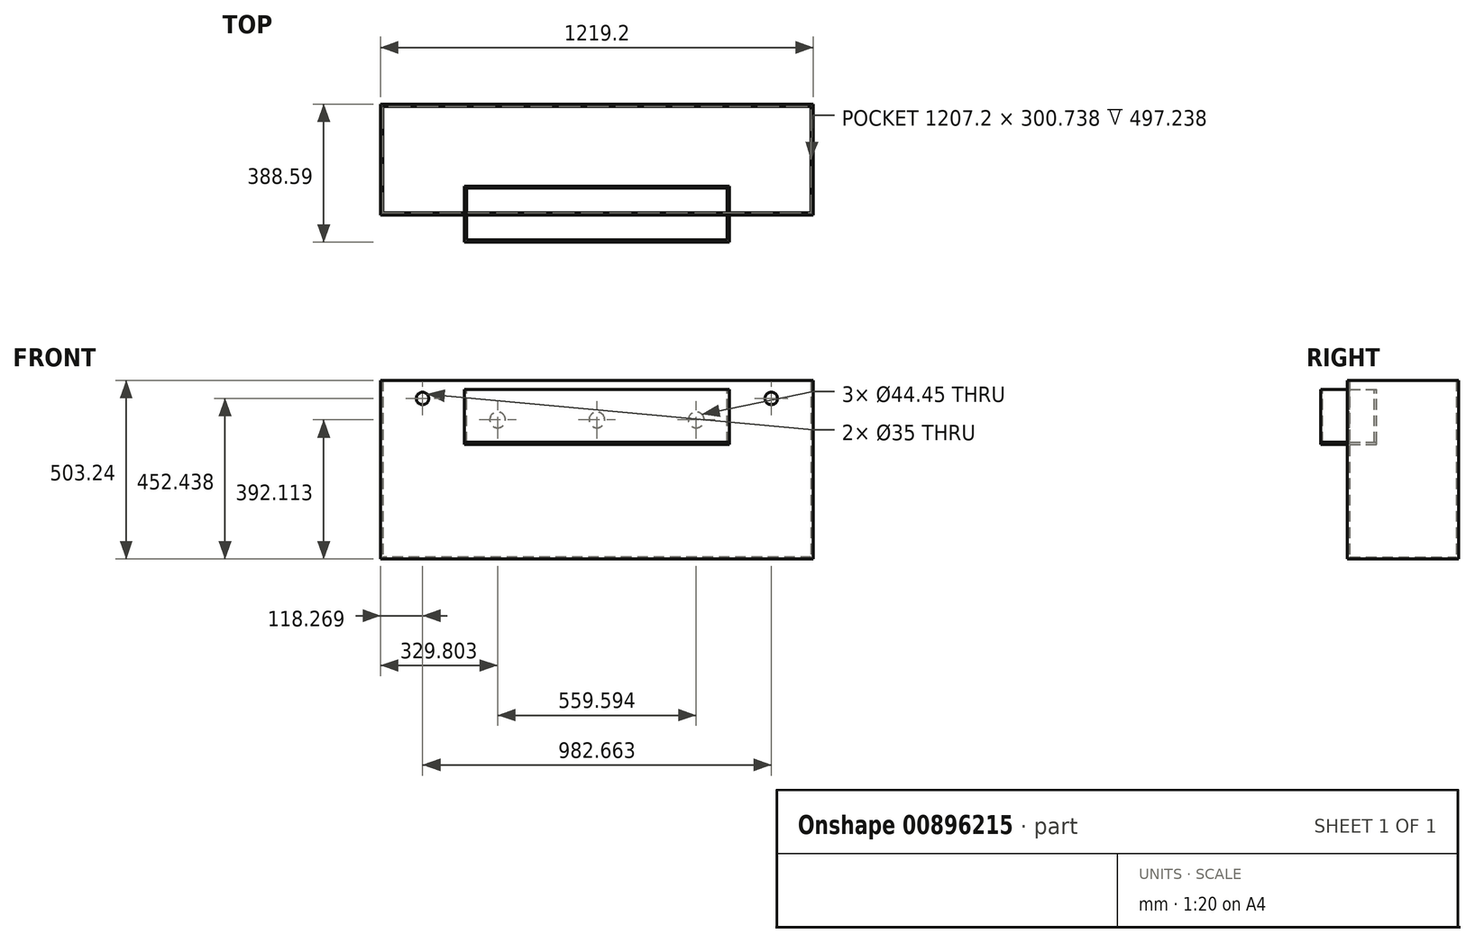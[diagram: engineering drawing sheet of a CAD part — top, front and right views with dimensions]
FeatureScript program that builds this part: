
annotation { "Feature Type Name" : "Feature", "Feature Type Description" : "" }
export const myFeature = defineFeature(function(context is Context, id is Id, definition is map)
    precondition{}
    {
        {
            var Q0;
            Q0=qCreatedBy(makeId("Top.planeOp"),FACE);
            var sketch = newSketch(context, id + "F0", { "sketchPlane" : qUnion([Q0])});
            skLineSegment(sketch, "E0.bottom", {"start": v(609.6, -156.37) * mm, "end": v(-609.6, -156.37) * mm});
            skLineSegment(sketch, "E0.top", {"start": v(609.6, 156.37) * mm, "end": v(-609.6, 156.37) * mm});
            skLineSegment(sketch, "E0.left", {"start": v(609.6, -156.37) * mm, "end": v(609.6, 156.37) * mm});
            skLineSegment(sketch, "E0.right", {"start": v(-609.6, -156.37) * mm, "end": v(-609.6, 156.37) * mm});
            skPoint(sketch, "E0.middle", {"position": v(0, 0) * mm});
            skSolve(sketch);
        }
        {
            var Q0;
            Q0=makeQuery(id+"F0.imprint","IMPRINT",FACE,{"disambiguationData":[TD([[makeQuery(id+"F0.imprint","IMPRINT",EDGE,{"derivedFrom":sQuery(id+"F0.wireOp",EDGE,"E0.bottom")}),-1.0]])]});
            extrude(context, id + "F1", {"entities" : qUnion([Q0]), "depth" : 503.24 * mm});
        }
        {
            var Q0;
            Q0=makeQuery(id+"F1.opExtrude","CAP_FACE",FACE,{"disambiguationData":[OSD([sQuery(id+"F0.wireOp",EDGE,"E0.bottom"),sQuery(id+"F0.wireOp",EDGE,"E0.top"),sQuery(id+"F0.wireOp",EDGE,"E0.left"),sQuery(id+"F0.wireOp",EDGE,"E0.right")])],"isStart":false});
            shell(context, id + "F2", {"entities" : qUnion([Q0]), "thickness" : 6 * mm});
        }
        {
            var Q0;
            Q0=makeQuery(id+"F1.opExtrude","SWEPT_FACE",FACE,{"disambiguationData":[OSD([sQuery(id+"F0.wireOp",EDGE,"E0.bottom")])]});
            var sketch = newSketch(context, id + "F3", { "sketchPlane" : qUnion([Q0])});
            skPoint(sketch, "E1", {"position": v(609.6, 414.34) * mm});
            skPoint(sketch, "E2", {"position": v(-609.6, 414.34) * mm});
            skLineSegment(sketch, "E3", {"start": v(-609.6, 414.34) * mm, "end": v(609.6, 414.34) * mm, "construction": true});
            skLineSegment(sketch, "E4", {"start": v(0, 503.24) * mm, "end": v(0, 0) * mm, "construction": true});
            skLineSegment(sketch, "E5", {"start": v(-609.6, 369.89) * mm, "end": v(609.6, 369.89) * mm, "construction": true});
            skLineSegment(sketch, "E6", {"start": v(-373.06, 503.24) * mm, "end": v(-373.06, 0) * mm, "construction": true});
            skLineSegment(sketch, "E7", {"start": v(373.06, 503.24) * mm, "end": v(373.06, 0) * mm, "construction": true});
            skLineSegment(sketch, "E8", {"start": v(0, 414.34) * mm, "end": v(0, 369.89) * mm, "construction": true});
            skPoint(sketch, "E9", {"position": v(0, 392.11) * mm});
            skLineSegment(sketch, "E10", {"start": v(-609.6, 392.11) * mm, "end": v(609.6, 392.11) * mm, "construction": true});
            skCircle(sketch, "E11", {"center": v(0, 392.11) * mm, "radius": 22.22 * mm});
            skLineSegment(sketch, "E12", {"start": v(0, 414.34) * mm, "end": v(-373.06, 414.34) * mm, "construction": true});
            skPoint(sketch, "E13", {"position": v(-186.53, 414.34) * mm});
            skLineSegment(sketch, "E14", {"start": v(-186.53, 414.34) * mm, "end": v(-186.53, 369.89) * mm, "construction": true});
            skLineSegment(sketch, "E15", {"start": v(0, 414.34) * mm, "end": v(373.06, 414.34) * mm, "construction": true});
            skPoint(sketch, "E16", {"position": v(186.53, 414.34) * mm});
            skLineSegment(sketch, "E17", {"start": v(186.53, 414.34) * mm, "end": v(186.53, 369.89) * mm, "construction": true});
            skLineSegment(sketch, "E18", {"start": v(-186.53, 414.34) * mm, "end": v(-373.06, 414.34) * mm, "construction": true});
            skPoint(sketch, "E19", {"position": v(-279.8, 414.34) * mm});
            skLineSegment(sketch, "E20", {"start": v(-279.8, 414.34) * mm, "end": v(-279.8, 369.89) * mm, "construction": true});
            skCircle(sketch, "E21", {"center": v(-279.8, 392.11) * mm, "radius": 22.23 * mm});
            skLineSegment(sketch, "E22", {"start": v(186.53, 414.34) * mm, "end": v(373.06, 414.34) * mm, "construction": true});
            skPoint(sketch, "E23", {"position": v(279.8, 414.34) * mm});
            skLineSegment(sketch, "E24", {"start": v(279.8, 414.34) * mm, "end": v(279.8, 369.89) * mm, "construction": true});
            skCircle(sketch, "E25", {"center": v(279.8, 392.11) * mm, "radius": 22.22 * mm});
            skLineSegment(sketch, "E26", {"start": v(-609.6, 328.61) * mm, "end": v(609.6, 328.61) * mm, "construction": true});
            skLineSegment(sketch, "E27", {"start": v(373.06, 503.24) * mm, "end": v(609.6, 503.24) * mm, "construction": true});
            skLineSegment(sketch, "E28", {"start": v(491.33, 503.24) * mm, "end": v(491.33, 0) * mm, "construction": true});
            skLineSegment(sketch, "E29", {"start": v(-609.6, 503.24) * mm, "end": v(-373.06, 503.24) * mm, "construction": true});
            skLineSegment(sketch, "E30", {"start": v(-491.33, 503.24) * mm, "end": v(-491.33, 0) * mm, "construction": true});
            skLineSegment(sketch, "E31", {"start": v(-609.6, 503.24) * mm, "end": v(-609.6, 414.34) * mm, "construction": true});
            skCircle(sketch, "E32", {"center": v(491.33, 452.44) * mm, "radius": 17.5 * mm});
            skLineSegment(sketch, "E33", {"start": v(-609.6, 452.44) * mm, "end": v(609.6, 452.44) * mm, "construction": true});
            skCircle(sketch, "E34", {"center": v(-491.33, 452.44) * mm, "radius": 17.5 * mm});
            skSolve(sketch);
        }
        {
            var Q0;
            Q0=makeQuery(id+"F1.opExtrude","CAP_FACE",FACE,{"disambiguationData":[OSD([sQuery(id+"F0.wireOp",EDGE,"E0.bottom"),sQuery(id+"F0.wireOp",EDGE,"E0.top"),sQuery(id+"F0.wireOp",EDGE,"E0.left"),sQuery(id+"F0.wireOp",EDGE,"E0.right")])],"isStart":false});
            var sketch = newSketch(context, id + "F4", { "sketchPlane" : qUnion([Q0])});
            skLineSegment(sketch, "E35", {"start": v(-603.6, -80.52) * mm, "end": v(603.6, -80.52) * mm, "construction": true});
            skPoint(sketch, "E36.0", {"position": v(373.06, -156.37) * mm});
            skPoint(sketch, "E37.0", {"position": v(-373.06, -156.37) * mm});
            skLineSegment(sketch, "E38", {"start": v(-373.06, -156.37) * mm, "end": v(-373.06, -80.52) * mm, "construction": true});
            skLineSegment(sketch, "E39", {"start": v(373.06, -156.37) * mm, "end": v(373.06, -80.52) * mm, "construction": true});
            skPoint(sketch, "E40", {"position": v(-373.06, -150.37) * mm});
            skPoint(sketch, "E41", {"position": v(-367.06, -150.37) * mm});
            skPoint(sketch, "E42", {"position": v(367.06, -150.37) * mm});
            skLineSegment(sketch, "E43", {"start": v(367.06, -150.37) * mm, "end": v(367.06, -80.52) * mm, "construction": true});
            skLineSegment(sketch, "E44.bottom", {"start": v(-373.06, -80.52) * mm, "end": v(373.06, -80.52) * mm});
            skLineSegment(sketch, "E44.top", {"start": v(-373.06, -74.52) * mm, "end": v(373.06, -74.52) * mm});
            skLineSegment(sketch, "E44.left", {"start": v(-373.06, -80.52) * mm, "end": v(-373.06, -74.52) * mm});
            skLineSegment(sketch, "E44.right", {"start": v(373.06, -80.52) * mm, "end": v(373.06, -74.52) * mm});
            skLineSegment(sketch, "E45.left", {"start": v(-373.06, -74.52) * mm, "end": v(-373.06, -80.52) * mm});
            skLineSegment(sketch, "E45.right", {"start": v(373.06, -74.52) * mm, "end": v(373.06, -80.52) * mm});
            skLineSegment(sketch, "E46.bottom", {"start": v(-367.06, -150.37) * mm, "end": v(-373.06, -150.37) * mm});
            skLineSegment(sketch, "E46.top", {"start": v(-367.06, -80.52) * mm, "end": v(-373.06, -80.52) * mm});
            skLineSegment(sketch, "E46.left", {"start": v(-367.06, -150.37) * mm, "end": v(-367.06, -80.52) * mm});
            skLineSegment(sketch, "E46.right", {"start": v(-373.06, -150.37) * mm, "end": v(-373.06, -80.52) * mm});
            skLineSegment(sketch, "E47.bottom", {"start": v(367.06, -150.37) * mm, "end": v(373.06, -150.37) * mm});
            skLineSegment(sketch, "E47.top", {"start": v(367.06, -80.52) * mm, "end": v(373.06, -80.52) * mm});
            skLineSegment(sketch, "E47.left", {"start": v(367.06, -150.37) * mm, "end": v(367.06, -80.52) * mm});
            skLineSegment(sketch, "E47.right", {"start": v(373.06, -150.37) * mm, "end": v(373.06, -80.52) * mm});
            skSolve(sketch);
        }
        {
            var Q0;
            Q0=makeQuery(id+"F4.imprint","IMPRINT",FACE,{"disambiguationData":[TD([[makeQuery(id+"F4.imprint","IMPRINT",EDGE,{"derivedFrom":sQuery(id+"F4.wireOp",EDGE,"E47.bottom")}),-1.0]])]});
            var Q1;
            Q1=makeQuery(id+"F4.imprint","IMPRINT",FACE,{"disambiguationData":[TD([[makeQuery(id+"F4.imprint","IMPRINT",EDGE,{"derivedFrom":sQuery(id+"F4.wireOp",EDGE,"E44.top")}),-1.0]])]});
            var Q2;
            Q2=makeQuery(id+"F4.imprint","IMPRINT",FACE,{"disambiguationData":[TD([[makeQuery(id+"F4.imprint","IMPRINT",EDGE,{"derivedFrom":sQuery(id+"F4.wireOp",EDGE,"E46.bottom")}),-1.0]])]});
            extrude(context, id + "F5", {"entities" : qUnion([Q0, Q1, Q2]), "oppositeDirection" : true, "depth" : 174.62 * mm});
        }
        {
            var Q0;
            Q0=makeQuery(id+"F5.opExtrude","CAP_FACE",FACE,{"disambiguationData":[OSD([sQuery(id+"F4.wireOp",EDGE,"E44.top"),sQuery(id+"F4.wireOp",EDGE,"E44.bottom"),sQuery(id+"F4.wireOp",EDGE,"E45.left"),sQuery(id+"F4.wireOp",EDGE,"E45.right"),sQuery(id+"F4.wireOp",EDGE,"E46.bottom"),sQuery(id+"F4.wireOp",EDGE,"E46.left"),sQuery(id+"F4.wireOp",EDGE,"E46.right"),sQuery(id+"F4.wireOp",EDGE,"E47.bottom"),sQuery(id+"F4.wireOp",EDGE,"E47.left"),sQuery(id+"F4.wireOp",EDGE,"E47.right")])],"isStart":true});
            extrude(context, id + "F6", {"entities" : qUnion([Q0]), "operationType" : NewBodyOperationType.REMOVE, "oppositeDirection" : true, "depth" : 25.4 * mm});
        }
        {
            var Q0;
            Q0=makeQuery(id+"F5.opExtrude","CAP_FACE",FACE,{"disambiguationData":[OSD([sQuery(id+"F4.wireOp",EDGE,"E44.top"),sQuery(id+"F4.wireOp",EDGE,"E44.bottom"),sQuery(id+"F4.wireOp",EDGE,"E45.left"),sQuery(id+"F4.wireOp",EDGE,"E45.right"),sQuery(id+"F4.wireOp",EDGE,"E46.bottom"),sQuery(id+"F4.wireOp",EDGE,"E46.left"),sQuery(id+"F4.wireOp",EDGE,"E46.right"),sQuery(id+"F4.wireOp",EDGE,"E47.bottom"),sQuery(id+"F4.wireOp",EDGE,"E47.left"),sQuery(id+"F4.wireOp",EDGE,"E47.right")])],"isStart":false});
            var sketch = newSketch(context, id + "F7", { "sketchPlane" : qUnion([Q0])});
            skLineSegment(sketch, "E48.bottom", {"start": v(-373.06, 150.37) * mm, "end": v(373.06, 150.37) * mm});
            skLineSegment(sketch, "E48.top", {"start": v(-373.06, 74.52) * mm, "end": v(373.06, 74.52) * mm});
            skLineSegment(sketch, "E48.left", {"start": v(-373.06, 150.37) * mm, "end": v(-373.06, 74.52) * mm});
            skLineSegment(sketch, "E48.right", {"start": v(373.06, 150.37) * mm, "end": v(373.06, 74.52) * mm});
            skSolve(sketch);
        }
        {
            var Q0;
            Q0=qSketchRegion(id+"F7",true);
            extrude(context, id + "F8", {"entities" : qUnion([Q0]), "depth" : 6 * mm});
        }
        {
            var Q0;
            Q0=makeQuery(id+"F3.imprint","IMPRINT",FACE,{"disambiguationData":[TD([[makeQuery(id+"F3.imprint","IMPRINT",EDGE,{"derivedFrom":sQuery(id+"F3.wireOp",EDGE,"E25")}),1.0]])]});
            var Q1;
            Q1=makeQuery(id+"F3.imprint","IMPRINT",FACE,{"disambiguationData":[TD([[makeQuery(id+"F3.imprint","IMPRINT",EDGE,{"derivedFrom":sQuery(id+"F3.wireOp",EDGE,"E11")}),1.0]])]});
            var Q2;
            Q2=makeQuery(id+"F3.imprint","IMPRINT",FACE,{"disambiguationData":[TD([[makeQuery(id+"F3.imprint","IMPRINT",EDGE,{"derivedFrom":sQuery(id+"F3.wireOp",EDGE,"E21")}),1.0]])]});
            var Q3;
            Q3=sQuery(id+"F3.wireOp",EDGE,"E21");
            var Q4;
            Q4=sQuery(id+"F3.wireOp",EDGE,"E11");
            var Q5;
            Q5=sQuery(id+"F3.wireOp",EDGE,"E25");
            var Q6;
            Q6=makeQuery(id+"F5.opExtrude","SWEPT_BODY",BODY,{"disambiguationData":[OSD([sQuery(id+"F4.wireOp",EDGE,"E44.top"),sQuery(id+"F4.wireOp",EDGE,"E44.bottom"),sQuery(id+"F4.wireOp",EDGE,"E45.left"),sQuery(id+"F4.wireOp",EDGE,"E45.right"),sQuery(id+"F4.wireOp",EDGE,"E46.bottom"),sQuery(id+"F4.wireOp",EDGE,"E46.left"),sQuery(id+"F4.wireOp",EDGE,"E46.right"),sQuery(id+"F4.wireOp",EDGE,"E47.bottom"),sQuery(id+"F4.wireOp",EDGE,"E47.left"),sQuery(id+"F4.wireOp",EDGE,"E47.right")])]});
            extrude(context, id + "F9", {"entities" : qUnion([Q0, Q1, Q2]), "operationType" : NewBodyOperationType.REMOVE, "surfaceEntities" : qUnion([Q3, Q4, Q5]), "endBound" : BoundingType.UP_TO_BODY, "oppositeDirection" : true, "endBoundEntityBody" : qUnion([Q6]), "depth" : 25.4 * mm});
        }
        {
            var Q0;
            Q0=makeQuery(id+"F3.imprint","IMPRINT",FACE,{"disambiguationData":[TD([[makeQuery(id+"F3.imprint","IMPRINT",EDGE,{"derivedFrom":sQuery(id+"F3.wireOp",EDGE,"E34")}),1.0]])]});
            var Q1;
            Q1=makeQuery(id+"F3.imprint","IMPRINT",FACE,{"disambiguationData":[TD([[makeQuery(id+"F3.imprint","IMPRINT",EDGE,{"derivedFrom":sQuery(id+"F3.wireOp",EDGE,"E32")}),1.0]])]});
            var Q2;
            Q2=sQuery(id+"F3.wireOp",EDGE,"E34");
            var Q3;
            Q3=sQuery(id+"F3.wireOp",EDGE,"E32");
            var Q4;
            Q4=makeQuery(id+"F1.opExtrude","SWEPT_BODY",BODY,{"disambiguationData":[OSD([sQuery(id+"F0.wireOp",EDGE,"E0.bottom"),sQuery(id+"F0.wireOp",EDGE,"E0.top"),sQuery(id+"F0.wireOp",EDGE,"E0.left"),sQuery(id+"F0.wireOp",EDGE,"E0.right")])]});
            extrude(context, id + "F10", {"entities" : qUnion([Q0, Q1]), "operationType" : NewBodyOperationType.REMOVE, "surfaceEntities" : qUnion([Q2, Q3]), "endBound" : BoundingType.UP_TO_BODY, "oppositeDirection" : true, "endBoundEntityBody" : qUnion([Q4]), "depth" : 25.4 * mm});
        }
        {
            var Q0;
            Q0=makeQuery(id+"F5.opExtrude","SWEPT_BODY",BODY,{"disambiguationData":[OSD([sQuery(id+"F4.wireOp",EDGE,"E44.top"),sQuery(id+"F4.wireOp",EDGE,"E44.bottom"),sQuery(id+"F4.wireOp",EDGE,"E45.left"),sQuery(id+"F4.wireOp",EDGE,"E45.right"),sQuery(id+"F4.wireOp",EDGE,"E46.bottom"),sQuery(id+"F4.wireOp",EDGE,"E46.left"),sQuery(id+"F4.wireOp",EDGE,"E46.right"),sQuery(id+"F4.wireOp",EDGE,"E47.bottom"),sQuery(id+"F4.wireOp",EDGE,"E47.left"),sQuery(id+"F4.wireOp",EDGE,"E47.right")])]});
            var Q1;
            Q1=makeQuery(id+"F8.opExtrude","SWEPT_BODY",BODY,{"disambiguationData":[OSD([sQuery(id+"F7.wireOp",EDGE,"E48.bottom"),sQuery(id+"F7.wireOp",EDGE,"E48.top"),sQuery(id+"F7.wireOp",EDGE,"E48.left"),sQuery(id+"F7.wireOp",EDGE,"E48.right")])]});
            var Q2;
            Q2=makeQuery(id+"F3.imprint","IMPRINT",FACE,{"disambiguationData":[TD([[makeQuery(id+"F3.imprint","IMPRINT",EDGE,{"derivedFrom":sQuery(id+"F3.wireOp",EDGE,"E11")}),-1.0]])]});
            mirror(context, id + "F11", {"entities" : qUnion([Q0, Q1]), "mirrorPlane" : qUnion([Q2])});
        }
        {
            var Q0;
            Q0=makeQuery(id+"F11.opPattern","COPY",BODY,{"derivedFrom":makeQuery(id+"F5.opExtrude","SWEPT_BODY",BODY,{"disambiguationData":[OSD([sQuery(id+"F4.wireOp",EDGE,"E44.top"),sQuery(id+"F4.wireOp",EDGE,"E44.bottom"),sQuery(id+"F4.wireOp",EDGE,"E45.left"),sQuery(id+"F4.wireOp",EDGE,"E45.right"),sQuery(id+"F4.wireOp",EDGE,"E46.bottom"),sQuery(id+"F4.wireOp",EDGE,"E46.left"),sQuery(id+"F4.wireOp",EDGE,"E46.right"),sQuery(id+"F4.wireOp",EDGE,"E47.bottom"),sQuery(id+"F4.wireOp",EDGE,"E47.left"),sQuery(id+"F4.wireOp",EDGE,"E47.right")])]}),"instanceName":"1"});
            var Q1;
            Q1=makeQuery(id+"F11.opPattern","COPY",BODY,{"derivedFrom":makeQuery(id+"F8.opExtrude","SWEPT_BODY",BODY,{"disambiguationData":[OSD([sQuery(id+"F7.wireOp",EDGE,"E48.bottom"),sQuery(id+"F7.wireOp",EDGE,"E48.top"),sQuery(id+"F7.wireOp",EDGE,"E48.left"),sQuery(id+"F7.wireOp",EDGE,"E48.right")])]}),"instanceName":"1"});
            transform(context, id + "F12", {"entities" : qUnion([Q0, Q1]), "transformType" : TransformType.TRANSLATION_3D, "dx" : 0 * mm, "dy" : 6 * mm, "dz" : 0 * mm, "makeCopy" : false});
        }
    });
